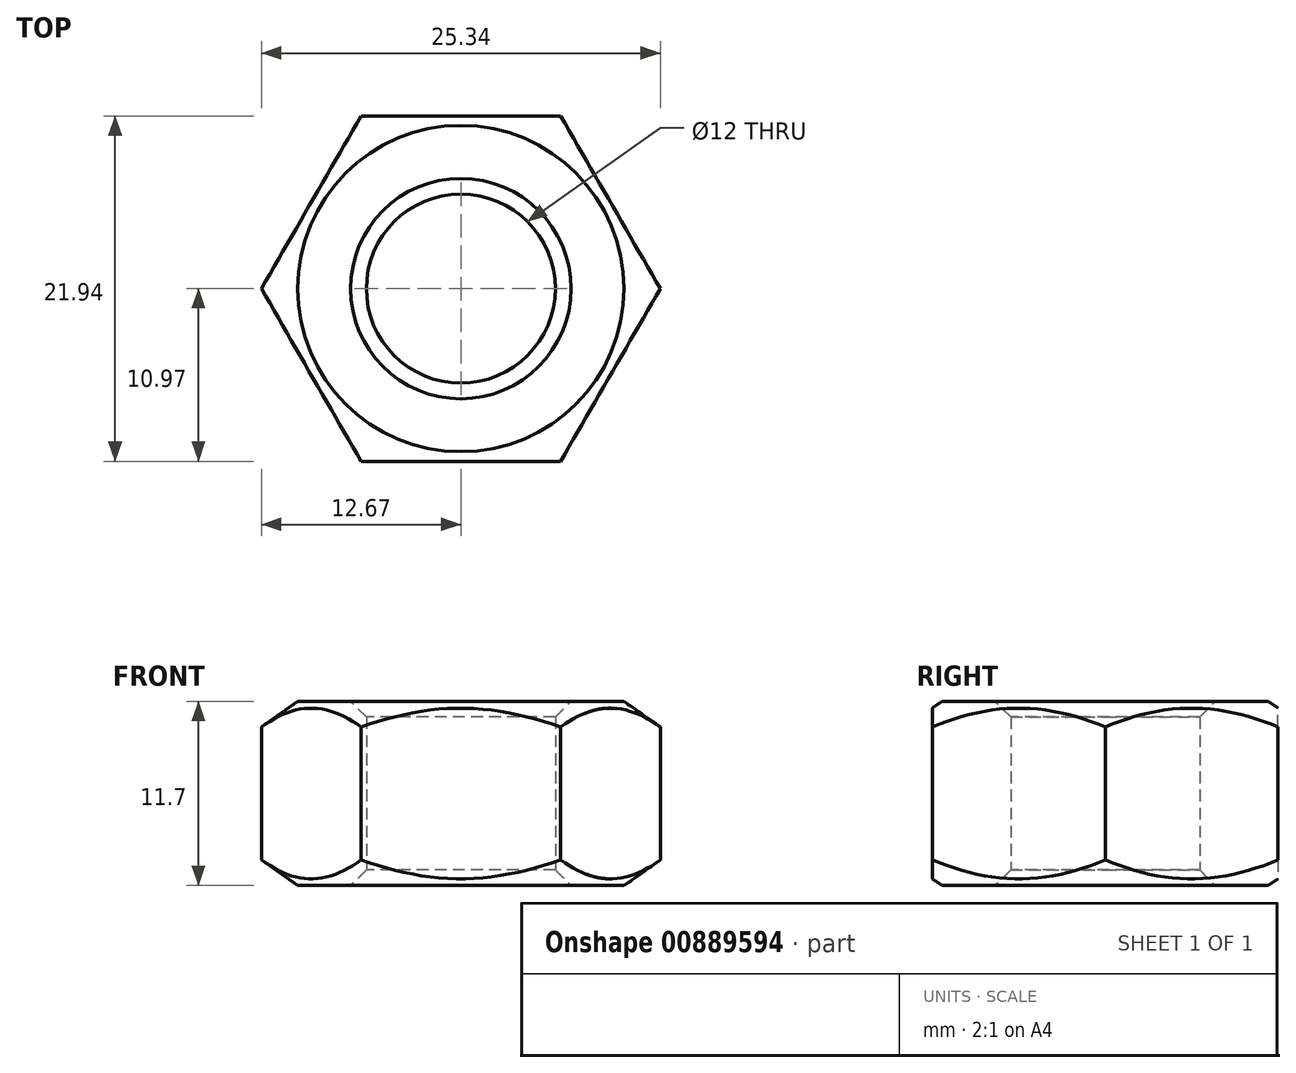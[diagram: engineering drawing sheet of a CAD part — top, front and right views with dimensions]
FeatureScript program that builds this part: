
annotation { "Feature Type Name" : "Feature", "Feature Type Description" : "" }
export const myFeature = defineFeature(function(context is Context, id is Id, definition is map)
    precondition{}
    {
        {
            var Q0;
            Q0=qCreatedBy(makeId("Top.planeOp"),FACE);
            var sketch = newSketch(context, id + "F0", { "sketchPlane" : qUnion([Q0])});
            skCircle(sketch, "E0", {"center": v(0, 0) * mm, "radius": 6 * mm});
            skCircle(sketch, "E1.cCircle", {"center": v(0, 0) * mm, "radius": 10.97 * mm, "construction": true});
            skLineSegment(sketch, "E1.0", {"start": v(-6.33, 10.97) * mm, "end": v(6.33, 10.97) * mm});
            skLineSegment(sketch, "E1.1", {"start": v(6.33, 10.97) * mm, "end": v(12.67, 0) * mm});
            skLineSegment(sketch, "E1.2", {"start": v(12.67, 0) * mm, "end": v(6.33, -10.97) * mm});
            skLineSegment(sketch, "E1.3", {"start": v(6.33, -10.97) * mm, "end": v(-6.33, -10.97) * mm});
            skLineSegment(sketch, "E1.4", {"start": v(-6.33, -10.97) * mm, "end": v(-12.67, 0) * mm});
            skLineSegment(sketch, "E1.5", {"start": v(-12.67, 0) * mm, "end": v(-6.33, 10.97) * mm});
            skPoint(sketch, "E1.0.midPoint", {"position": v(0, 10.97) * mm});
            skSolve(sketch);
        }
        {
            var Q0;
            Q0=makeQuery(id+"F0.imprint","IMPRINT",FACE,{"disambiguationData":[TD([[makeQuery(id+"F0.imprint","IMPRINT",EDGE,{"derivedFrom":sQuery(id+"F0.wireOp",EDGE,"E0")}),-1.0]])]});
            extrude(context, id + "F1", {"entities" : qUnion([Q0]), "depth" : 11.7 * mm, "offsetDistance" : 25 * mm});
        }
        {
            var Q0;
            Q0=qCreatedBy(makeId("Right.planeOp"),FACE);
            var sketch = newSketch(context, id + "F2", { "sketchPlane" : qUnion([Q0])});
            skLineSegment(sketch, "E2", {"start": v(-18.18, 5.85) * mm, "end": v(19.84, 5.85) * mm, "construction": true});
            skLineSegment(sketch, "E3", {"start": v(9.65, 12.2) * mm, "end": v(13.28, 9.65) * mm});
            skLineSegment(sketch, "E4", {"start": v(13.28, 9.65) * mm, "end": v(13.28, 12.61) * mm});
            skLineSegment(sketch, "E5", {"start": v(13.28, 12.61) * mm, "end": v(9.65, 12.2) * mm});
            skLineSegment(sketch, "E6.MirrorCS", {"start": v(9.65, -0.5) * mm, "end": v(13.28, 2.05) * mm});
            skLineSegment(sketch, "E7.MirrorCS", {"start": v(13.28, -0.91) * mm, "end": v(9.65, -0.5) * mm});
            skLineSegment(sketch, "E8.MirrorCS", {"start": v(13.28, 2.05) * mm, "end": v(13.28, -0.91) * mm});
            skLineSegment(sketch, "E9", {"start": v(0, 19.7) * mm, "end": v(0, -7.73) * mm});
            skSolve(sketch);
        }
        {
            var Q0;
            Q0=makeQuery(id+"F2.imprint","IMPRINT",FACE,{"disambiguationData":[TD([[makeQuery(id+"F2.imprint","IMPRINT",EDGE,{"derivedFrom":sQuery(id+"F2.wireOp",EDGE,"E3")}),1.0]])]});
            var Q1;
            Q1=makeQuery(id+"F2.imprint","IMPRINT",FACE,{"disambiguationData":[TD([[makeQuery(id+"F2.imprint","IMPRINT",EDGE,{"derivedFrom":sQuery(id+"F2.wireOp",EDGE,"E6.MirrorCS")}),-1.0]])]});
            var Q2;
            Q2=sQuery(id+"F2.wireOp",EDGE,"E9");
            revolve(context, id + "F3", {"operationType" : NewBodyOperationType.REMOVE, "surfaceOperationType" : NewSurfaceOperationType.NEW, "entities" : qUnion([Q0, Q1]), "axis" : qUnion([Q2]), "revolveType" : RevolveType.FULL, "oppositeDirection" : true});
        }
        {
            var Q0;
            Q0=makeQuery(id+"F1.opExtrude","CAP_EDGE",EDGE,{"disambiguationData":[OSD([sQuery(id+"F0.wireOp",EDGE,"E0")])],"isStart":false});
            var Q1;
            Q1=makeQuery(id+"F1.opExtrude","CAP_EDGE",EDGE,{"disambiguationData":[OSD([sQuery(id+"F0.wireOp",EDGE,"E0")])],"isStart":true});
            chamfer(context, id + "F4", {"entities" : qUnion([Q0, Q1]), "width" : 1 * mm, "tangentPropagation" : true});
        }
    });
